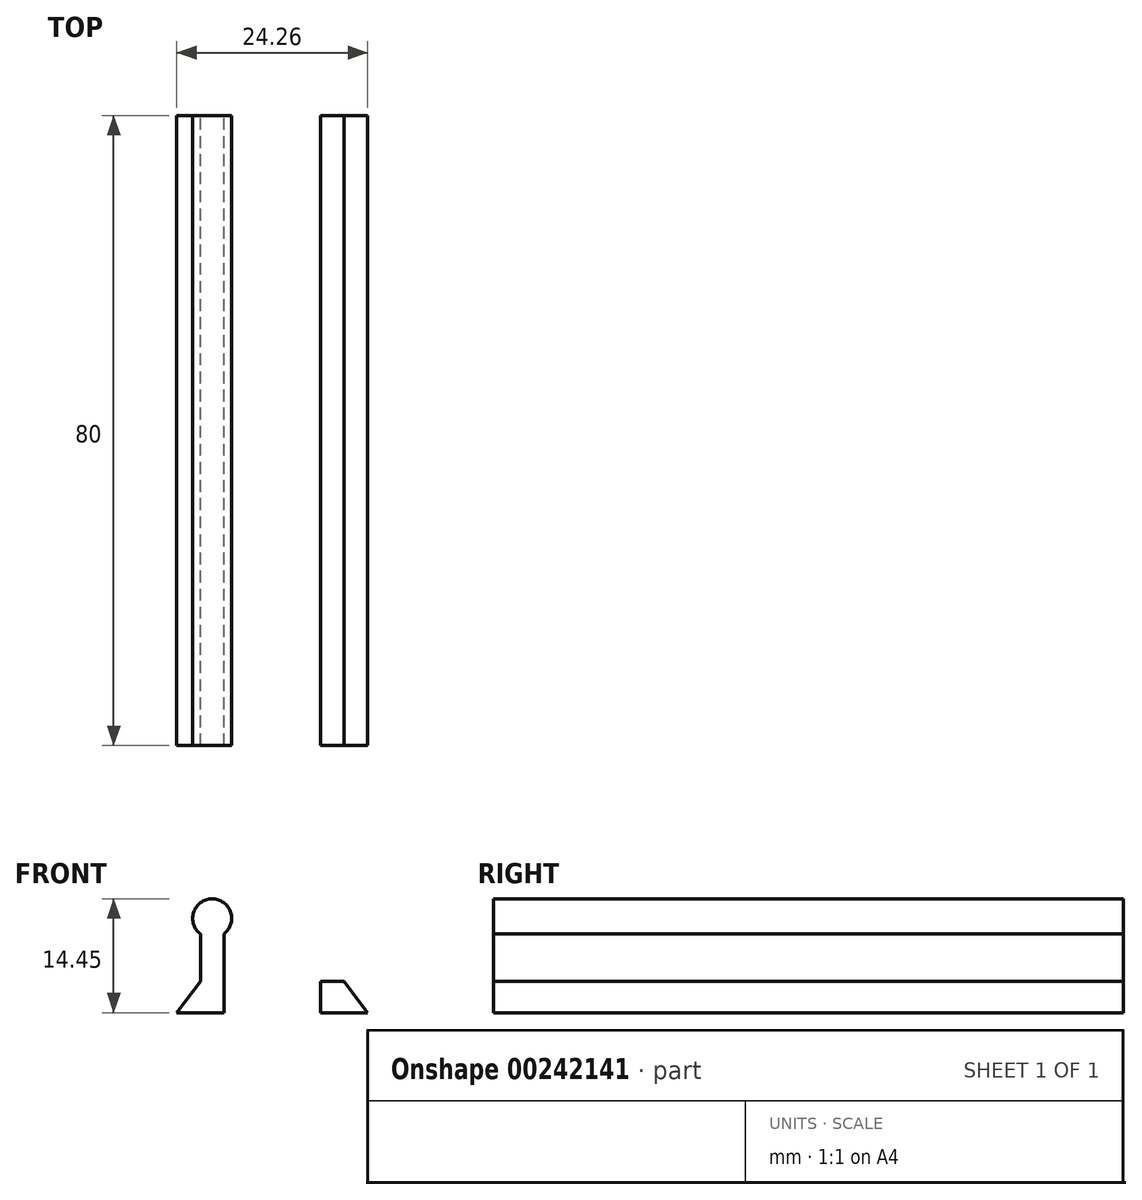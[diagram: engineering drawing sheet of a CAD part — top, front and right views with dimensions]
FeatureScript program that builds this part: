
annotation { "Feature Type Name" : "Feature", "Feature Type Description" : "" }
export const myFeature = defineFeature(function(context is Context, id is Id, definition is map)
    precondition{}
    {
        {
            var Q0;
            Q0=qCreatedBy(makeId("Front.planeOp"),FACE);
            var sketch = newSketch(context, id + "F0", { "sketchPlane" : qUnion([Q0])});
            skArc(sketch, "E0", {"start": v(14.04, -6.4) * mm, "mid": v(12.54, -1.95) * mm, "end": v(11.04, -6.4) * mm});
            skLineSegment(sketch, "E1", {"start": v(11.04, -6.4) * mm, "end": v(11.04, -12.4) * mm});
            skLineSegment(sketch, "E2", {"start": v(14.04, -6.4) * mm, "end": v(14.04, -12.4) * mm});
            skLineSegment(sketch, "E3", {"start": v(11.04, -12.4) * mm, "end": v(14.04, -12.4) * mm});
            skLineSegment(sketch, "E4", {"start": v(11.04, -12.4) * mm, "end": v(8.04, -16.4) * mm});
            skLineSegment(sketch, "E5", {"start": v(14.04, -16.4) * mm, "end": v(14.04, -12.4) * mm});
            skLineSegment(sketch, "E6", {"start": v(8.04, -16.4) * mm, "end": v(14.04, -16.4) * mm});
            skLineSegment(sketch, "E7", {"start": v(20.17, -4.43) * mm, "end": v(20.17, 4.28) * mm, "construction": true});
            skArc(sketch, "E8.MirrorCS", {"start": v(26.3, -6.4) * mm, "mid": v(27.8, -1.95) * mm, "end": v(29.3, -6.4) * mm});
            skLineSegment(sketch, "E9.MirrorCS", {"start": v(26.3, -6.4) * mm, "end": v(26.3, -12.4) * mm});
            skLineSegment(sketch, "E10.MirrorCS", {"start": v(29.3, -12.4) * mm, "end": v(26.3, -12.4) * mm});
            skLineSegment(sketch, "E11.MirrorCS", {"start": v(29.3, -6.4) * mm, "end": v(29.3, -12.4) * mm});
            skLineSegment(sketch, "E12.MirrorCS", {"start": v(29.3, -12.4) * mm, "end": v(32.3, -16.4) * mm});
            skLineSegment(sketch, "E13.MirrorCS", {"start": v(32.3, -16.4) * mm, "end": v(26.3, -16.4) * mm});
            skLineSegment(sketch, "E14.MirrorCS", {"start": v(26.3, -16.4) * mm, "end": v(26.3, -12.4) * mm});
            skSolve(sketch);
        }
        {
            var Q0;
            Q0=makeQuery(id+"F0.imprint","IMPRINT",FACE,{"disambiguationData":[TD([[makeQuery(id+"F0.imprint","IMPRINT",EDGE,{"derivedFrom":sQuery(id+"F0.wireOp",EDGE,"E3")}),-1.0]])]});
            var Q1;
            Q1=makeQuery(id+"F0.imprint","IMPRINT",FACE,{"disambiguationData":[TD([[makeQuery(id+"F0.imprint","IMPRINT",EDGE,{"derivedFrom":sQuery(id+"F0.wireOp",EDGE,"E8.MirrorCS")}),-1.0]])]});
            var Q2;
            Q2=makeQuery(id+"F0.imprint","IMPRINT",FACE,{"disambiguationData":[TD([[makeQuery(id+"F0.imprint","IMPRINT",EDGE,{"derivedFrom":sQuery(id+"F0.wireOp",EDGE,"E10.MirrorCS")}),1.0]])]});
            var Q3;
            Q3=makeQuery(id+"F0.imprint","IMPRINT",FACE,{"disambiguationData":[TD([[makeQuery(id+"F0.imprint","IMPRINT",EDGE,{"derivedFrom":sQuery(id+"F0.wireOp",EDGE,"E0")}),1.0]])]});
            extrude(context, id + "F1", {"entities" : qUnion([Q0, Q1, Q2, Q3]), "depth" : 80 * mm});
        }
    });
